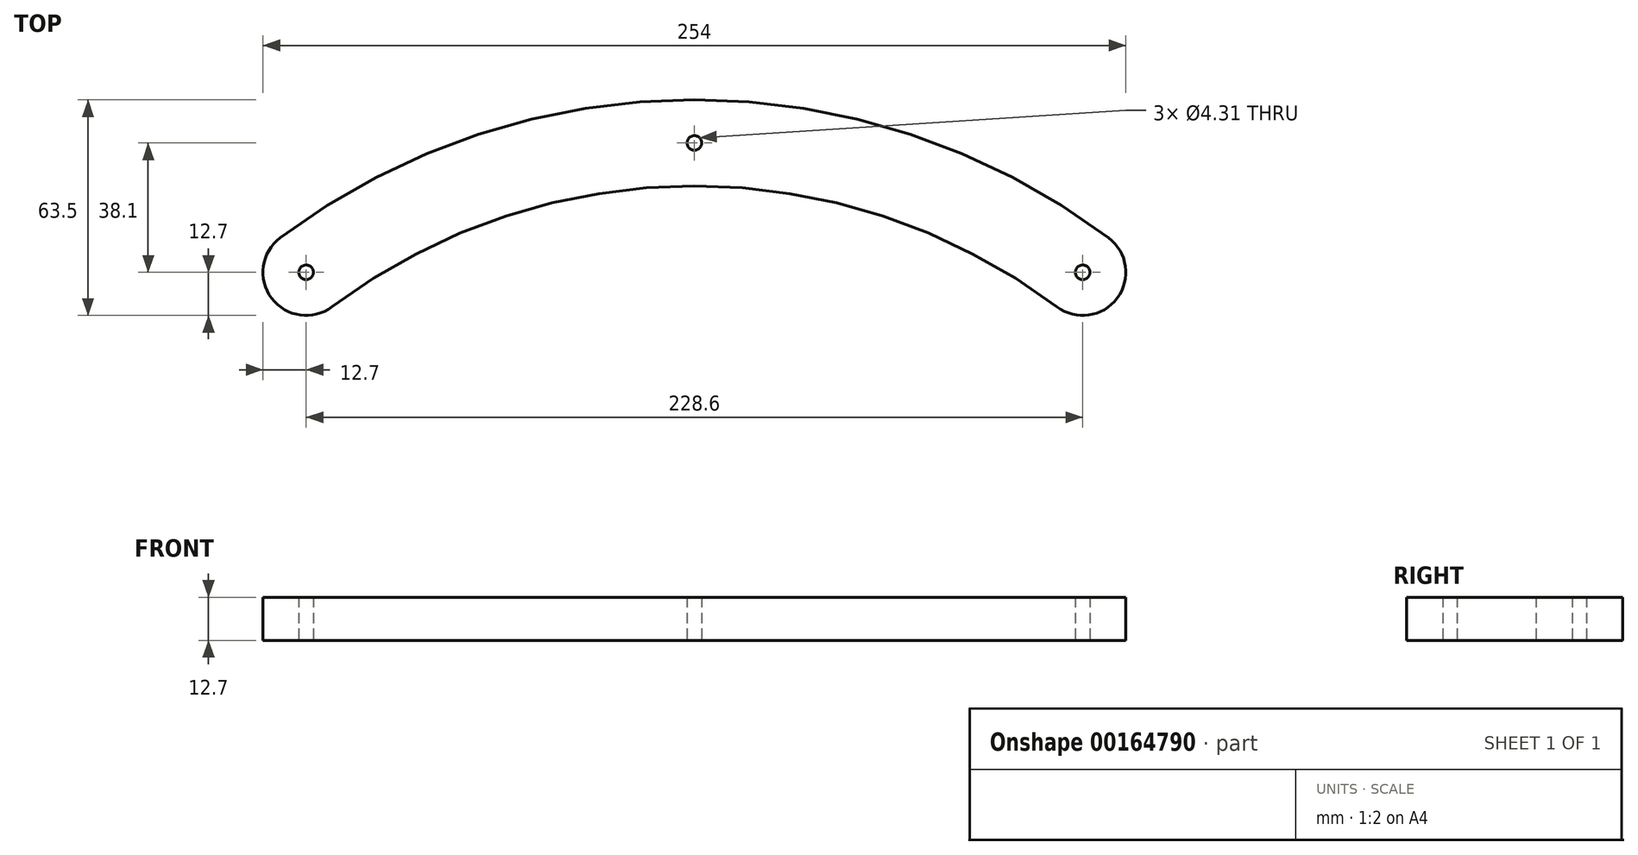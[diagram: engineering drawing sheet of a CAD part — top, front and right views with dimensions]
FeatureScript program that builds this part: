
annotation { "Feature Type Name" : "Feature", "Feature Type Description" : "" }
export const myFeature = defineFeature(function(context is Context, id is Id, definition is map)
    precondition{}
    {
        {
            var Q0;
            Q0=qCreatedBy(makeId("Top.planeOp"),FACE);
            var sketch = newSketch(context, id + "F0", { "sketchPlane" : qUnion([Q0])});
            skLineSegment(sketch, "E0.bottom", {"start": v(0, 0) * mm, "end": v(254, 0) * mm, "construction": true});
            skLineSegment(sketch, "E0.left", {"start": v(0, 0) * mm, "end": v(0, 12.7) * mm, "construction": true});
            skLineSegment(sketch, "E0.right", {"start": v(254, 0) * mm, "end": v(254, 12.7) * mm, "construction": true});
            skArc(sketch, "E1", {"start": v(5.08, 22.86) * mm, "mid": v(2.54, 5.08) * mm, "end": v(20.32, 2.54) * mm});
            skArc(sketch, "E2", {"start": v(233.68, 2.54) * mm, "mid": v(127, 38.1) * mm, "end": v(20.32, 2.54) * mm});
            skArc(sketch, "E3", {"start": v(233.68, 2.54) * mm, "mid": v(251.46, 5.08) * mm, "end": v(248.92, 22.86) * mm});
            skArc(sketch, "E4", {"start": v(248.92, 22.86) * mm, "mid": v(127, 63.5) * mm, "end": v(5.08, 22.86) * mm});
            skLineSegment(sketch, "E5", {"start": v(127, 0) * mm, "end": v(127, -139.7) * mm, "construction": true});
            skCircle(sketch, "E6", {"center": v(12.7, 12.7) * mm, "radius": 2.15 * mm});
            skCircle(sketch, "E7", {"center": v(241.3, 12.7) * mm, "radius": 2.15 * mm});
            skLineSegment(sketch, "E8", {"start": v(127, 0) * mm, "end": v(127, 38.1) * mm, "construction": true});
            skLineSegment(sketch, "E9", {"start": v(127, 38.1) * mm, "end": v(127, 63.5) * mm, "construction": true});
            skCircle(sketch, "E10", {"center": v(127, 50.8) * mm, "radius": 2.15 * mm});
            skSolve(sketch);
        }
        {
            var Q0;
            Q0 = qSketchRegion(id + "F0", true);
            extrude(context, id + "F1", {"entities" : qUnion([Q0]), "depth" : 12.7 * mm});
        }
    });
